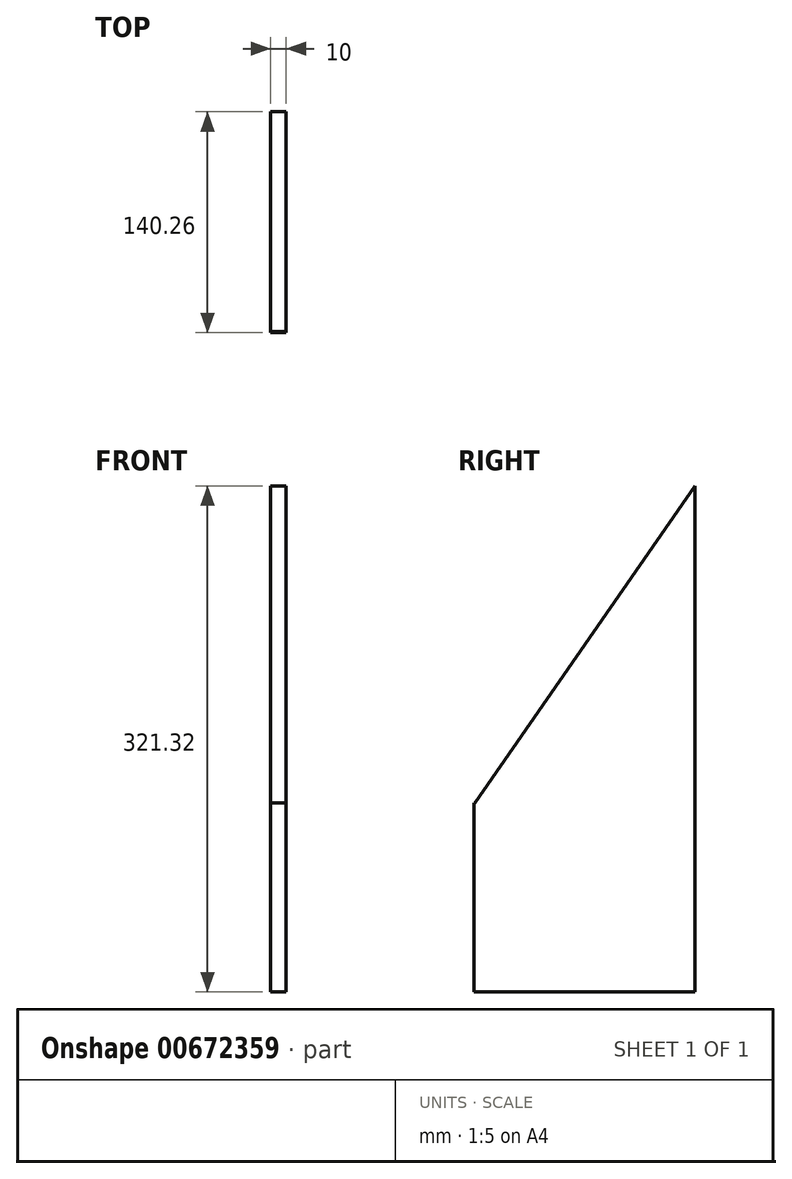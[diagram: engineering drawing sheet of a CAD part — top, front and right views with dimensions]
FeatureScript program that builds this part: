
annotation { "Feature Type Name" : "Feature", "Feature Type Description" : "" }
export const myFeature = defineFeature(function(context is Context, id is Id, definition is map)
    precondition{}
    {
        {
            var Q0;
            Q0=qCreatedBy(makeId("Right.planeOp"),FACE);
            var sketch = newSketch(context, id + "F0", { "sketchPlane" : qUnion([Q0])});
            skLineSegment(sketch, "E0.bottom", {"start": v(-140.26, 0) * mm, "end": v(-139.63, 0) * mm});
            skLineSegment(sketch, "E0.top", {"start": v(-140.26, 120) * mm, "end": v(-139.63, 120) * mm});
            skLineSegment(sketch, "E0.left", {"start": v(-139.63, 0) * mm, "end": v(-139.63, 120) * mm});
            skLineSegment(sketch, "E0.right", {"start": v(-140.26, 0) * mm, "end": v(-140.26, 120) * mm});
            skLineSegment(sketch, "E1.bottom", {"start": v(0, 0) * mm, "end": v(0, 0) * mm});
            skLineSegment(sketch, "E1.top", {"start": v(0, 321.32) * mm, "end": v(0, 321.32) * mm});
            skLineSegment(sketch, "E1.left", {"start": v(0, 0) * mm, "end": v(0, 321.32) * mm});
            skLineSegment(sketch, "E1.right", {"start": v(0, 0) * mm, "end": v(0, 321.32) * mm});
            skLineSegment(sketch, "E2", {"start": v(0, 321.32) * mm, "end": v(-139.63, 120) * mm});
            skLineSegment(sketch, "E3", {"start": v(-140.26, 0) * mm, "end": v(0, 0) * mm});
            skSolve(sketch);
        }
        {
            var Q0;
            Q0 = qSketchRegion(id + "F0", true);
            extrude(context, id + "F1", {"entities" : qUnion([Q0]), "depth" : 10 * mm, "offsetDistance" : 25 * mm});
        }
    });
